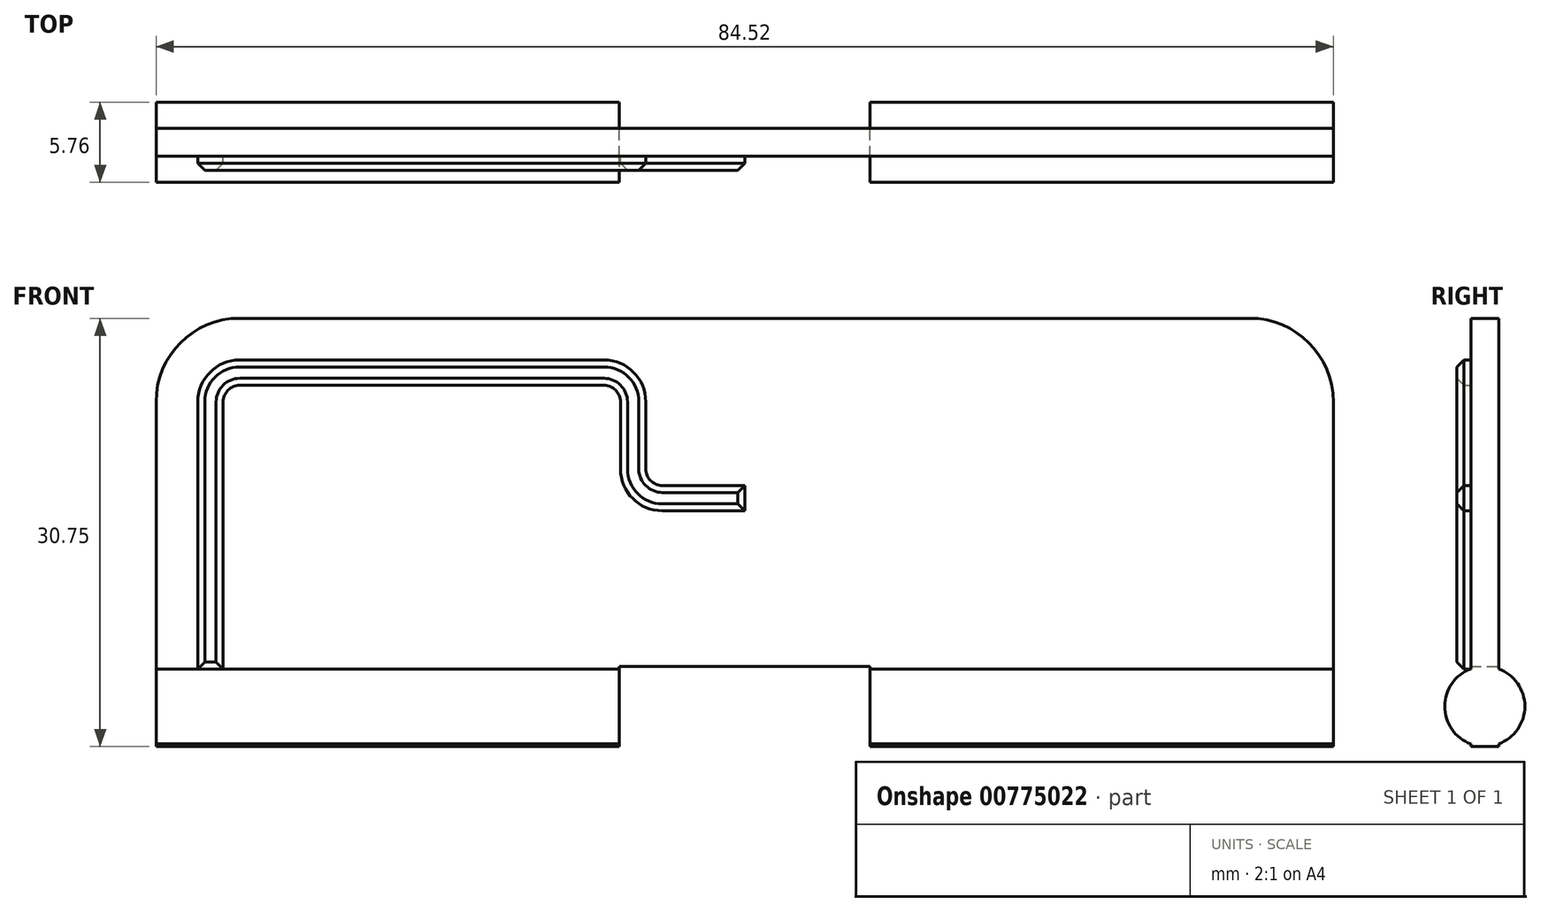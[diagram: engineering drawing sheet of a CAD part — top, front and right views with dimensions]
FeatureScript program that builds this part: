
annotation { "Feature Type Name" : "Feature", "Feature Type Description" : "" }
export const myFeature = defineFeature(function(context is Context, id is Id, definition is map)
    precondition{}
    {
        {
            var Q0;
            Q0=qCreatedBy(makeId("Front.planeOp"),FACE);
            var sketch = newSketch(context, id + "F0", { "sketchPlane" : qUnion([Q0])});
            skLineSegment(sketch, "E0.bottom", {"start": v(-36.26, 12.5) * mm, "end": v(36.26, 12.5) * mm});
            skLineSegment(sketch, "E0.top", {"start": v(-42.26, -12.5) * mm, "end": v(42.26, -12.5) * mm});
            skLineSegment(sketch, "E0.left", {"start": v(-42.26, 6.5) * mm, "end": v(-42.26, -12.5) * mm});
            skLineSegment(sketch, "E0.right", {"start": v(42.26, 6.5) * mm, "end": v(42.26, -12.5) * mm});
            skPoint(sketch, "E0.middle", {"position": v(0, 0) * mm});
            skLineSegment(sketch, "E1.bottom", {"start": v(-42.26, -12.5) * mm, "end": v(-9, -12.5) * mm});
            skLineSegment(sketch, "E1.top", {"start": v(-42.26, -18.25) * mm, "end": v(-9, -18.25) * mm});
            skLineSegment(sketch, "E1.left", {"start": v(-42.26, -12.5) * mm, "end": v(-42.26, -18.25) * mm});
            skLineSegment(sketch, "E1.right", {"start": v(-9, -12.5) * mm, "end": v(-9, -18.25) * mm});
            skLineSegment(sketch, "E2.bottom", {"start": v(42.26, -12.5) * mm, "end": v(9, -12.5) * mm});
            skLineSegment(sketch, "E2.top", {"start": v(42.26, -18.25) * mm, "end": v(9, -18.25) * mm});
            skLineSegment(sketch, "E2.left", {"start": v(42.26, -12.5) * mm, "end": v(42.26, -18.25) * mm});
            skLineSegment(sketch, "E2.right", {"start": v(9, -12.5) * mm, "end": v(9, -18.25) * mm});
            skPoint(sketch, "E3.visualSharp", {"position": v(-42.26, 12.5) * mm});
            skArc(sketch, "E3.filletArc", {"start": v(-36.26, 12.5) * mm, "mid": v(-40.5, 10.74) * mm, "end": v(-42.26, 6.5) * mm});
            skPoint(sketch, "E4.visualSharp", {"position": v(42.26, 12.5) * mm});
            skArc(sketch, "E4.filletArc", {"start": v(42.26, 6.5) * mm, "mid": v(40.5, 10.74) * mm, "end": v(36.26, 12.5) * mm});
            skLineSegment(sketch, "E5.bottom", {"start": v(-9, -12.5) * mm, "end": v(9, -12.5) * mm});
            skLineSegment(sketch, "E6", {"start": v(9, -12.5) * mm, "end": v(3.67, -11.07) * mm});
            skLineSegment(sketch, "E7", {"start": v(-9, -12.5) * mm, "end": v(-3.67, -11.07) * mm});
            skLineSegment(sketch, "E8", {"start": v(3.67, -11.07) * mm, "end": v(-3.67, -11.07) * mm});
            skSolve(sketch);
        }
        {
            var Q0;
            Q0=qSketchRegion(id+"F0",true);
            extrude(context, id + "F1", {"entities" : qUnion([Q0]), "depth" : 2 * mm, "offsetDistance" : 25 * mm});
        }
        {
            var Q0;
            Q0=makeQuery(id+"F1.opExtrude","SWEPT_FACE",FACE,{"disambiguationData":[OSD([sQuery(id+"F0.wireOp",EDGE,"E0.left"),sQuery(id+"F0.wireOp",EDGE,"E1.left")])]});
            var sketch = newSketch(context, id + "F2", { "sketchPlane" : qUnion([Q0])});
            skPoint(sketch, "E9.0", {"position": v(2, -15.38) * mm});
            skLineSegment(sketch, "E10.0", {"start": v(2, -12.5) * mm, "end": v(2, -18.25) * mm});
            skPoint(sketch, "E11.0", {"position": v(1, -18.25) * mm});
            skCircle(sketch, "E12", {"center": v(1, -15.38) * mm, "radius": 2.88 * mm});
            skSolve(sketch);
        }
        {
            var Q0;
            Q0=qSketchRegion(id+"F2",true);
            var Q1;
            Q1=sQuery(id+"F2.wireOp",EDGE,"zfLG92Hy-l4Sj-bWKc-iMt7-KAgflosJrh2A");
            var Q2;
            Q2=makeQuery(id+"F1.opExtrude","SWEPT_FACE",FACE,{"disambiguationData":[OSD([sQuery(id+"F0.wireOp",EDGE,"E1.right")])]});
            extrude(context, id + "F3", {"entities" : qUnion([Q0]), "operationType" : NewBodyOperationType.ADD, "surfaceEntities" : qUnion([Q1]), "endBound" : BoundingType.UP_TO_SURFACE, "oppositeDirection" : true, "depth" : 25 * mm, "endBoundEntityFace" : qUnion([Q2]), "offsetDistance" : 25 * mm});
        }
        {
            var Q0;
            {var subQ0=sQuery(id+"F0.wireOp",EDGE,"E4.filletArc");var subQ1=sQuery(id+"F0.wireOp",EDGE,"E1.right");var subQ2=sQuery(id+"F0.wireOp",EDGE,"E3.filletArc");var subQ3=sQuery(id+"F0.wireOp",EDGE,"E2.right");var subQ4=sQuery(id+"F0.wireOp",EDGE,"E2.top");var subQ5=sQuery(id+"F0.wireOp",EDGE,"E5.bottom");var subQ6=sQuery(id+"F0.wireOp",EDGE,"E0.bottom");var subQ8=sQuery(id+"F0.wireOp",EDGE,"E1.left");var subQ9=sQuery(id+"F0.wireOp",EDGE,"E0.left");var subQ10=sQuery(id+"F0.wireOp",EDGE,"E2.left");var subQ11=sQuery(id+"F0.wireOp",EDGE,"E0.right");Q0=makeQuery(id+"F3.boolean.opBoolean","SPLIT",FACE,{"disambiguationData":[TD([makeQuery(id+"F1.opExtrude","SWEPT_FACE",FACE,{"disambiguationData":[OSD([subQ6])]})])],"derivedFrom":makeQuery(id+"F1.opExtrude","CAP_FACE",FACE,{"disambiguationData":[OSD([subQ6,subQ9,subQ11,sQuery(id+"F0.wireOp",EDGE,"E1.top"),subQ8,subQ1,subQ4,subQ10,subQ3,subQ2,subQ0,subQ5])],"isStart":false})});}
            var sketch = newSketch(context, id + "F4", { "sketchPlane" : qUnion([Q0])});
            skArc(sketch, "E13.0", {"start": v(-36.26, 12.5) * mm, "mid": v(-40.5, 10.74) * mm, "end": v(-42.26, 6.5) * mm});
            skLineSegment(sketch, "E14.0", {"start": v(-42.26, 6.5) * mm, "end": v(-42.26, -12.68) * mm});
            skLineSegment(sketch, "E15.0", {"start": v(-36.26, 12.5) * mm, "end": v(36.26, 12.5) * mm});
            skArc(sketch, "E16.0", {"start": v(-36.26, 9.5) * mm, "mid": v(-38.38, 8.62) * mm, "end": v(-39.26, 6.5) * mm});
            skLineSegment(sketch, "E17.bottom", {"start": v(-39.26, 6.5) * mm, "end": v(-37.45, 6.5) * mm});
            skLineSegment(sketch, "E17.top", {"start": v(-39.26, -12.68) * mm, "end": v(-37.45, -12.68) * mm});
            skLineSegment(sketch, "E17.left", {"start": v(-39.26, 6.5) * mm, "end": v(-39.26, -12.68) * mm});
            skLineSegment(sketch, "E17.right", {"start": v(-37.45, 6.5) * mm, "end": v(-37.45, -12.68) * mm});
            skArc(sketch, "E18", {"start": v(-36.26, 7.69) * mm, "mid": v(-37.1, 7.34) * mm, "end": v(-37.45, 6.5) * mm});
            skLineSegment(sketch, "E19.bottom", {"start": v(-36.26, 9.5) * mm, "end": v(-10.1, 9.5) * mm});
            skLineSegment(sketch, "E19.top", {"start": v(-36.26, 7.69) * mm, "end": v(-10.1, 7.69) * mm});
            skLineSegment(sketch, "E19.left", {"start": v(-36.26, 9.5) * mm, "end": v(-36.26, 7.69) * mm});
            skLineSegment(sketch, "E19.right", {"start": v(-10.1, 9.5) * mm, "end": v(-10.1, 7.69) * mm});
            skArc(sketch, "E20", {"start": v(-7.1, 6.5) * mm, "mid": v(-7.98, 8.62) * mm, "end": v(-10.1, 9.5) * mm});
            skArc(sketch, "E21", {"start": v(-8.91, 6.5) * mm, "mid": v(-9.26, 7.34) * mm, "end": v(-10.1, 7.69) * mm});
            skLineSegment(sketch, "E22.bottom", {"start": v(-7.1, 6.5) * mm, "end": v(-8.91, 6.5) * mm});
            skLineSegment(sketch, "E22.top", {"start": v(-7.1, 1.67) * mm, "end": v(-8.91, 1.67) * mm});
            skLineSegment(sketch, "E22.left", {"start": v(-7.1, 6.5) * mm, "end": v(-7.1, 1.67) * mm});
            skLineSegment(sketch, "E22.right", {"start": v(-8.91, 6.5) * mm, "end": v(-8.91, 1.67) * mm});
            skArc(sketch, "E23", {"start": v(-7.1, 1.67) * mm, "mid": v(-6.75, 0.84) * mm, "end": v(-5.91, 0.49) * mm});
            skArc(sketch, "E24", {"start": v(-8.91, 1.67) * mm, "mid": v(-8.03, -0.45) * mm, "end": v(-5.91, -1.33) * mm});
            skLineSegment(sketch, "E25.bottom", {"start": v(-5.91, 0.49) * mm, "end": v(0, 0.49) * mm});
            skLineSegment(sketch, "E25.top", {"start": v(-5.91, -1.33) * mm, "end": v(0, -1.33) * mm});
            skLineSegment(sketch, "E25.left", {"start": v(-5.91, 0.49) * mm, "end": v(-5.91, -1.33) * mm});
            skLineSegment(sketch, "E25.right", {"start": v(0, 0.49) * mm, "end": v(0, -1.33) * mm});
            skSolve(sketch);
        }
        {
            var Q0;
            Q0=makeQuery(id+"F1.opExtrude","SWEPT_FACE",FACE,{"disambiguationData":[OSD([sQuery(id+"F0.wireOp",EDGE,"E0.right"),sQuery(id+"F0.wireOp",EDGE,"E2.left")])]});
            var sketch = newSketch(context, id + "F5", { "sketchPlane" : qUnion([Q0])});
            skLineSegment(sketch, "E26.0.0", {"start": v(0, -12.68) * mm, "end": v(0, -12.5) * mm});
            skLineSegment(sketch, "E26.0.1", {"start": v(0, -12.5) * mm, "end": v(-2, -12.5) * mm});
            skLineSegment(sketch, "E26.0.2", {"start": v(-2, -12.5) * mm, "end": v(-2, -12.68) * mm});
            skLineSegment(sketch, "E26.0.4", {"start": v(-2, -18.25) * mm, "end": v(-2, -20.57) * mm});
            skLineSegment(sketch, "E26.0.5", {"start": v(-2, -18.25) * mm, "end": v(0, -18.25) * mm});
            skLineSegment(sketch, "E26.0.6", {"start": v(0, -18.25) * mm, "end": v(0, -18.07) * mm});
            skArc(sketch, "E26.0.7", {"start": v(0, -12.68) * mm, "mid": v(1.88, -15.38) * mm, "end": v(0, -18.07) * mm});
            skArc(sketch, "E27.0.3", {"start": v(-2, -18.07) * mm, "mid": v(-3.88, -15.38) * mm, "end": v(-2, -12.68) * mm});
            skLineSegment(sketch, "E27.0.4", {"start": v(-2, -18.07) * mm, "end": v(-2, -18.25) * mm});
            skSolve(sketch);
        }
        {
            var Q0;
            Q0=qSketchRegion(id+"F5",true);
            var Q1;
            Q1=makeQuery(id+"F1.opExtrude","SWEPT_FACE",FACE,{"disambiguationData":[OSD([sQuery(id+"F0.wireOp",EDGE,"E2.right")])]});
            extrude(context, id + "F6", {"entities" : qUnion([Q0]), "operationType" : NewBodyOperationType.ADD, "endBound" : BoundingType.UP_TO_SURFACE, "oppositeDirection" : true, "depth" : 25 * mm, "endBoundEntityFace" : qUnion([Q1]), "offsetDistance" : 25 * mm});
        }
        {
            var Q0;
            Q0=makeQuery(id+"F4.imprint","IMPRINT",FACE,{"disambiguationData":[TD([[makeQuery(id+"F4.imprint","IMPRINT",EDGE,{"derivedFrom":sQuery(id+"F4.wireOp",EDGE,"E17.bottom")}),-1.0]])]});
            var Q1;
            Q1=makeQuery(id+"F4.imprint","IMPRINT",FACE,{"disambiguationData":[TD([[makeQuery(id+"F4.imprint","IMPRINT",EDGE,{"derivedFrom":sQuery(id+"F4.wireOp",EDGE,"E16.0")}),1.0]])]});
            var Q2;
            Q2=makeQuery(id+"F4.imprint","IMPRINT",FACE,{"disambiguationData":[TD([[makeQuery(id+"F4.imprint","IMPRINT",EDGE,{"derivedFrom":sQuery(id+"F4.wireOp",EDGE,"E19.bottom")}),-1.0]])]});
            var Q3;
            Q3=makeQuery(id+"F4.imprint","IMPRINT",FACE,{"disambiguationData":[TD([[makeQuery(id+"F4.imprint","IMPRINT",EDGE,{"derivedFrom":sQuery(id+"F4.wireOp",EDGE,"E19.right")}),1.0]])]});
            var Q4;
            Q4=makeQuery(id+"F4.imprint","IMPRINT",FACE,{"disambiguationData":[TD([[makeQuery(id+"F4.imprint","IMPRINT",EDGE,{"derivedFrom":sQuery(id+"F4.wireOp",EDGE,"E22.bottom")}),1.0]])]});
            var Q5;
            Q5=makeQuery(id+"F4.imprint","IMPRINT",FACE,{"disambiguationData":[TD([[makeQuery(id+"F4.imprint","IMPRINT",EDGE,{"derivedFrom":sQuery(id+"F4.wireOp",EDGE,"E25.bottom")}),-1.0]])]});
            var Q6;
            Q6=makeQuery(id+"F4.imprint","IMPRINT",FACE,{"disambiguationData":[TD([[makeQuery(id+"F4.imprint","IMPRINT",EDGE,{"derivedFrom":sQuery(id+"F4.wireOp",EDGE,"E22.top")}),1.0]])]});
            extrude(context, id + "F7", {"entities" : qUnion([Q0, Q1, Q2, Q3, Q4, Q5, Q6]), "operationType" : NewBodyOperationType.ADD, "depth" : 1 * mm, "offsetDistance" : 25 * mm});
        }
        {
            var Q0;
            {var subQ0=sQuery(id+"F4.wireOp",EDGE,"E25.right");var subQ1=sQuery(id+"F4.wireOp",EDGE,"E25.top");var subQ2=sQuery(id+"F4.wireOp",EDGE,"E25.bottom");var subQ3=sQuery(id+"F4.wireOp",EDGE,"E24");var subQ4=sQuery(id+"F4.wireOp",EDGE,"E23");var subQ5=sQuery(id+"F4.wireOp",EDGE,"E22.right");var subQ6=sQuery(id+"F4.wireOp",EDGE,"E22.left");var subQ7=sQuery(id+"F4.wireOp",EDGE,"E21");var subQ8=sQuery(id+"F4.wireOp",EDGE,"E20");var subQ9=sQuery(id+"F4.wireOp",EDGE,"E19.top");var subQ10=sQuery(id+"F4.wireOp",EDGE,"E19.bottom");var subQ11=sQuery(id+"F4.wireOp",EDGE,"E18");var subQ12=sQuery(id+"F4.wireOp",EDGE,"E17.right");var subQ13=sQuery(id+"F4.wireOp",EDGE,"E17.left");var subQ14=sQuery(id+"F4.wireOp",EDGE,"E17.top");var subQ15=sQuery(id+"F4.wireOp",EDGE,"E16.0");Q0=makeQuery(id+"FafhX5HSumuEd5C_1.1.F7.boolean.opBoolean","MERGE",FACE,{"derivedFrom":[makeQuery(id+"F7.opExtrude","CAP_FACE",FACE,{"disambiguationData":[OSD([subQ15,subQ14,subQ13,subQ12,subQ11,subQ10,subQ9,subQ8,subQ7,subQ6,subQ5,subQ4,subQ3,subQ2,subQ1,subQ0])],"isStart":false}),makeQuery(id+"FafhX5HSumuEd5C_1.1.F7.opExtrude","CAP_FACE",FACE,{"disambiguationData":[OSD([subQ15,subQ14,subQ13,subQ12,subQ11,subQ10,subQ9,subQ8,subQ7,subQ6,subQ5,subQ4,subQ3,subQ2,subQ1,subQ0])],"isStart":false})]});}
            chamfer(context, id + "F8", {"entities" : qUnion([Q0]), "width" : .5 * mm, "tangentPropagation" : true});
        }
    });
